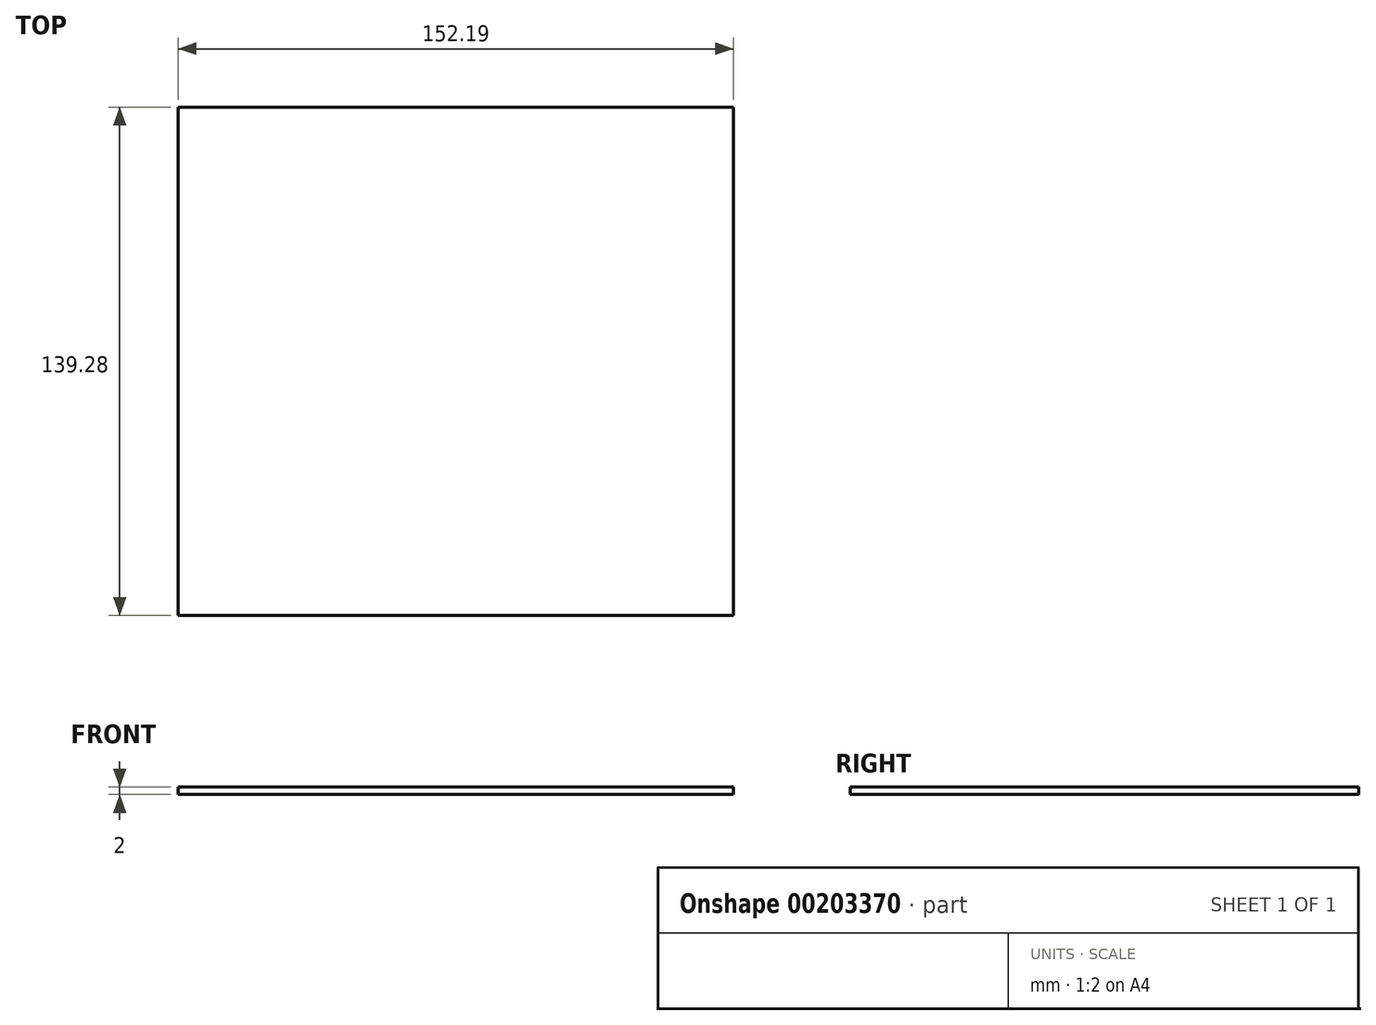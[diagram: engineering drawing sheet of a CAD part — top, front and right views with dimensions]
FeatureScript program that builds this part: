
annotation { "Feature Type Name" : "Feature", "Feature Type Description" : "" }
export const myFeature = defineFeature(function(context is Context, id is Id, definition is map)
    precondition{}
    {
        {
            var Q0;
            Q0=qCreatedBy(makeId("Top.planeOp"),FACE);
            var sketch = newSketch(context, id + "F0", { "sketchPlane" : qUnion([Q0])});
            skLineSegment(sketch, "E0.bottom", {"start": v(0, 0) * mm, "end": v(-152.2, 0) * mm});
            skLineSegment(sketch, "E0.top", {"start": v(0, 139.28) * mm, "end": v(-152.2, 139.28) * mm});
            skLineSegment(sketch, "E0.left", {"start": v(0, 0) * mm, "end": v(0, 139.28) * mm});
            skLineSegment(sketch, "E0.right", {"start": v(-152.2, 0) * mm, "end": v(-152.2, 139.28) * mm});
            skSolve(sketch);
        }
        {
            var Q0;
            Q0=makeQuery(id+"F0.imprint","IMPRINT",FACE,{"disambiguationData":[TD([[makeQuery(id+"F0.imprint","IMPRINT",EDGE,{"derivedFrom":sQuery(id+"F0.wireOp",EDGE,"E0.bottom")}),-1.0]])]});
            extrude(context, id + "F1", {"entities" : qUnion([Q0]), "depth" : 2 * mm});
        }
    });
